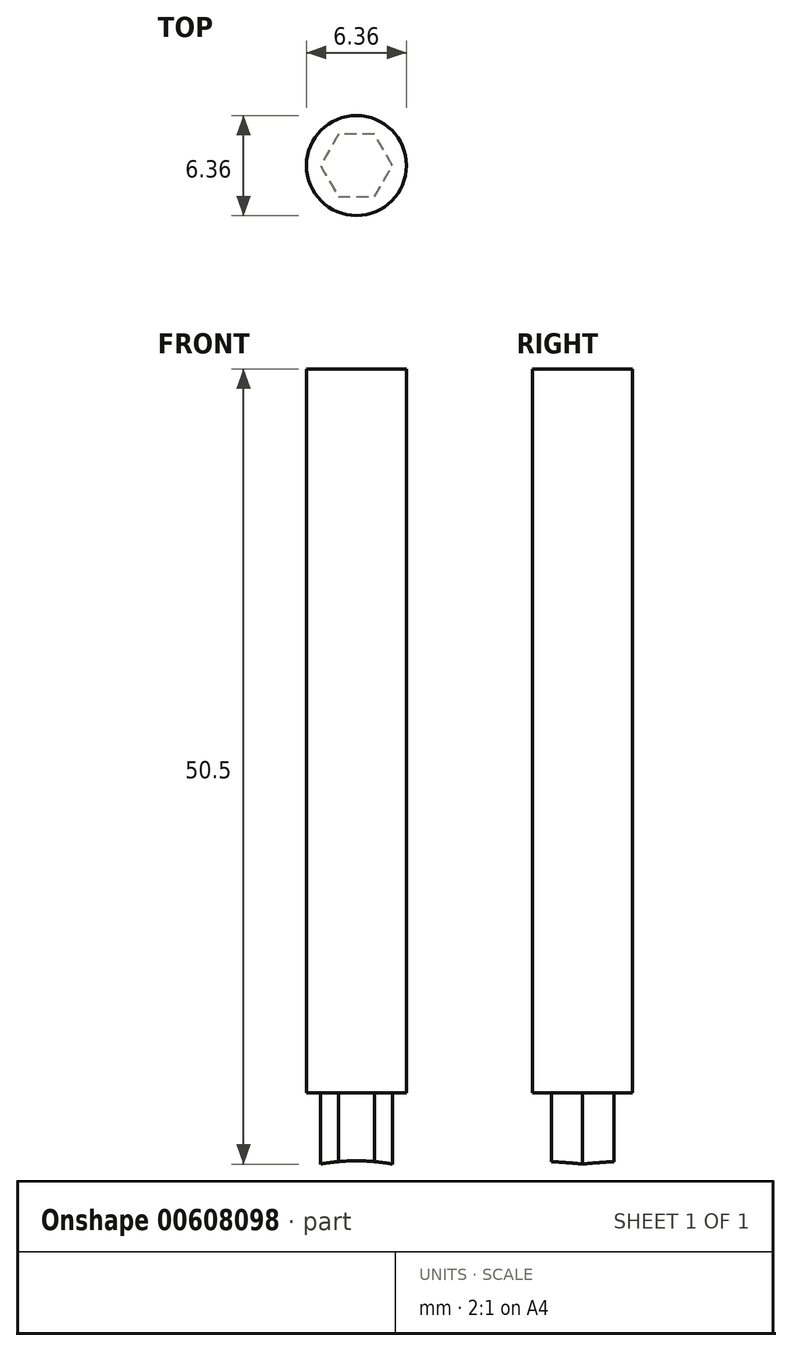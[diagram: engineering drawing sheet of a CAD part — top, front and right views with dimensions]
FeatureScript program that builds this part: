
annotation { "Feature Type Name" : "Feature", "Feature Type Description" : "" }
export const myFeature = defineFeature(function(context is Context, id is Id, definition is map)
    precondition{}
    {
        {
            var Q0;
            Q0=qCreatedBy(makeId("Front.planeOp"),FACE);
            var sketch = newSketch(context, id + "F0", { "sketchPlane" : qUnion([Q0])});
            skLineSegment(sketch, "E0", {"start": v(0, 0) * mm, "end": v(0, 63.81) * mm, "construction": true});
            skLineSegment(sketch, "E1", {"start": v(3.18, 0) * mm, "end": v(3.18, 50.8) * mm});
            skLineSegment(sketch, "E2", {"start": v(3.18, 50.8) * mm, "end": v(0, 50.8) * mm});
            skLineSegment(sketch, "E3", {"start": v(0, 50.8) * mm, "end": v(0, 0) * mm});
            skLineSegment(sketch, "E4", {"start": v(3.18, 0) * mm, "end": v(0, 0) * mm});
            skSolve(sketch);
        }
        {
            var Q0;
            Q0 = qSketchRegion(id + "F0", true);
            var Q1;
            Q1=sQuery(id+"F0.wireOp",EDGE,"E0");
            revolve(context, id + "F1", {"entities" : qUnion([Q0]), "axis" : qUnion([Q1]), "revolveType" : RevolveType.FULL});
        }
        {
            var Q0;
            Q0=makeQuery(id+"F1.opRevolve","SWEPT_FACE",FACE,{"disambiguationData":[OSD([sQuery(id+"F0.wireOp",EDGE,"E4")])]});
            var sketch = newSketch(context, id + "F2", { "sketchPlane" : qUnion([Q0])});
            skCircle(sketch, "E5.cCircle", {"center": v(0, 0) * mm, "radius": 1.98 * mm, "construction": true});
            skLineSegment(sketch, "E5.0", {"start": v(-1.15, 1.98) * mm, "end": v(1.15, 1.98) * mm});
            skLineSegment(sketch, "E5.1", {"start": v(1.15, 1.98) * mm, "end": v(2.3, 0) * mm});
            skLineSegment(sketch, "E5.2", {"start": v(2.3, 0) * mm, "end": v(1.15, -1.98) * mm});
            skLineSegment(sketch, "E5.3", {"start": v(1.15, -1.98) * mm, "end": v(-1.15, -1.98) * mm});
            skLineSegment(sketch, "E5.4", {"start": v(-1.15, -1.98) * mm, "end": v(-2.3, 0) * mm});
            skLineSegment(sketch, "E5.5", {"start": v(-2.3, 0) * mm, "end": v(-1.15, 1.98) * mm});
            skPoint(sketch, "E5.0.midPoint", {"position": v(0, 1.98) * mm});
            skCircle(sketch, "E6", {"center": v(0, 0) * mm, "radius": 4.76 * mm});
            skSolve(sketch);
        }
        {
            var Q0;
            Q0 = qSketchRegion(id + "F2", true);
            extrude(context, id + "F3", {"entities" : qUnion([Q0]), "operationType" : NewBodyOperationType.REMOVE, "oppositeDirection" : true, "depth" : 4.83 * mm, "offsetDistance" : 25.4 * mm});
        }
        {
            var Q0;
            Q0=qCreatedBy(makeId("Front.planeOp"),FACE);
            var sketch = newSketch(context, id + "F4", { "sketchPlane" : qUnion([Q0])});
            skCircle(sketch, "E7", {"center": v(0, -12.2) * mm, "radius": 12.7 * mm});
            skSolve(sketch);
        }
        {
            var Q0;
            Q0 = qSketchRegion(id + "F4", true);
            extrude(context, id + "F5", {"entities" : qUnion([Q0]), "operationType" : NewBodyOperationType.REMOVE, "endBound" : BoundingType.THROUGH_ALL, "oppositeDirection" : true, "depth" : 25.4 * mm, "offsetDistance" : 25.4 * mm, "hasSecondDirection" : true, "secondDirectionBound" : BoundingType.THROUGH_ALL, "secondDirectionOppositeDirection" : false, "secondDirectionDepth" : 25.4 * mm});
        }
    });
